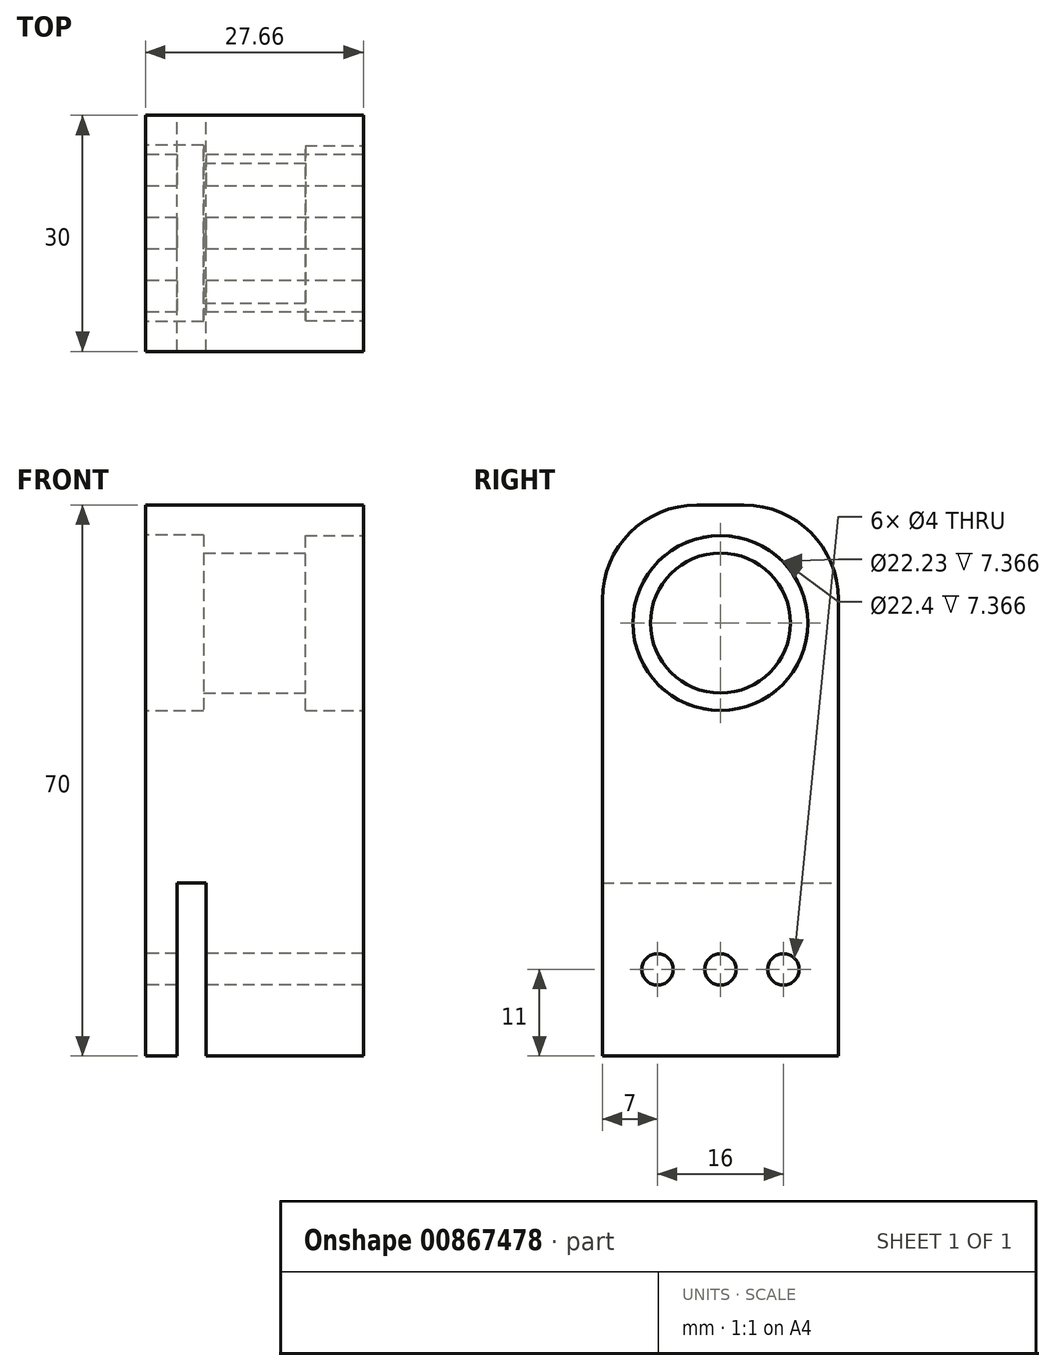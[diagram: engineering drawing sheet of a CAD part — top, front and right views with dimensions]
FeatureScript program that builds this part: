
annotation { "Feature Type Name" : "Feature", "Feature Type Description" : "" }
export const myFeature = defineFeature(function(context is Context, id is Id, definition is map)
    precondition{}
    {
        {
            var Q0;
            Q0=qCreatedBy(makeId("Front.planeOp"),FACE);
            var sketch = newSketch(context, id + "F0", { "sketchPlane" : qUnion([Q0])});
            skLineSegment(sketch, "E0.bottom", {"start": v(13.83, -27.5) * mm, "end": v(-13.82, -27.5) * mm});
            skLineSegment(sketch, "E0.top", {"start": v(13.82, 27.5) * mm, "end": v(-13.83, 27.5) * mm});
            skLineSegment(sketch, "E0.left", {"start": v(13.83, -27.5) * mm, "end": v(13.82, 27.5) * mm});
            skLineSegment(sketch, "E0.right", {"start": v(-13.82, -27.5) * mm, "end": v(-13.83, 27.5) * mm});
            skPoint(sketch, "E0.middle", {"position": v(0, 0) * mm});
            skLineSegment(sketch, "E1.bottom", {"start": v(-13.82, -27.5) * mm, "end": v(-9.82, -27.5) * mm});
            skLineSegment(sketch, "E1.top", {"start": v(-13.82, -5.5) * mm, "end": v(-9.82, -5.5) * mm, "construction": true});
            skLineSegment(sketch, "E1.left", {"start": v(-13.82, -27.5) * mm, "end": v(-13.82, -5.5) * mm});
            skLineSegment(sketch, "E1.right", {"start": v(-9.82, -27.5) * mm, "end": v(-9.82, -5.5) * mm});
            skLineSegment(sketch, "E2.bottom", {"start": v(-9.82, -27.5) * mm, "end": v(-6.17, -27.5) * mm});
            skLineSegment(sketch, "E2.top", {"start": v(-9.82, -5.5) * mm, "end": v(-6.17, -5.5) * mm});
            skLineSegment(sketch, "E2.right", {"start": v(-6.17, -27.5) * mm, "end": v(-6.17, -5.5) * mm});
            skLineSegment(sketch, "E3.bottom", {"start": v(-13.83, 27.5) * mm, "end": v(13.82, 27.5) * mm});
            skLineSegment(sketch, "E3.top", {"start": v(-13.83, 42.5) * mm, "end": v(13.82, 42.5) * mm});
            skLineSegment(sketch, "E3.left", {"start": v(-13.83, 27.5) * mm, "end": v(-13.83, 42.5) * mm});
            skLineSegment(sketch, "E3.right", {"start": v(13.82, 27.5) * mm, "end": v(13.82, 42.5) * mm});
            skSolve(sketch);
        }
        {
            var Q0;
            {var subQ1=sQuery(id+"F0.wireOp",EDGE,"E0.top");Q0=makeQuery(id+"F0.imprint","IMPRINT",FACE,{"disambiguationData":[TD([[makeQuery(id+"F0.imprint","IMPRINT",EDGE,{"derivedFrom":subQ1}),1.0]])]});}
            var Q1;
            Q1=makeQuery(id+"F0.imprint","IMPRINT",FACE,{"disambiguationData":[TD([[makeQuery(id+"F0.imprint","IMPRINT",EDGE,{"derivedFrom":sQuery(id+"F0.wireOp",EDGE,"E0.top")}),-1.0]])]});
            extrude(context, id + "F1", {"entities" : qUnion([Q0, Q1]), "endBound" : BoundingType.SYMMETRIC, "depth" : 30 * mm, "offsetDistance" : 25 * mm});
        }
        {
            var Q0;
            Q0=makeQuery(id+"F1.opExtrude","SWEPT_FACE",FACE,{"disambiguationData":[OSD([sQuery(id+"F0.wireOp",EDGE,"E0.left"),sQuery(id+"F0.wireOp",EDGE,"E3.right")])]});
            var sketch = newSketch(context, id + "F2", { "sketchPlane" : qUnion([Q0])});
            skLineSegment(sketch, "E4", {"start": v(0, 42.5) * mm, "end": v(0, 27.5) * mm});
            skCircle(sketch, "E5", {"center": v(0, 27.5) * mm, "radius": 11.11 * mm});
            skCircle(sketch, "E6", {"center": v(0, 27.5) * mm, "radius": 8.9 * mm});
            skSolve(sketch);
        }
        {
            var Q0;
            Q0=makeQuery(id+"F2.imprint","IMPRINT",FACE,{"disambiguationData":[TD([[makeQuery(id+"F2.imprint","IMPRINT",EDGE,{"derivedFrom":sQuery(id+"F2.wireOp",EDGE,"E5")}),1.0]])]});
            extrude(context, id + "F3", {"entities" : qUnion([Q0]), "operationType" : NewBodyOperationType.REMOVE, "oppositeDirection" : true, "depth" : 7.37 * mm, "offsetDistance" : 25 * mm});
        }
        {
            var Q0;
            Q0=makeQuery(id+"F3.boolean.opBoolean","SPLIT",FACE,{"disambiguationData":[TD([makeQuery(id+"F3.opExtrude","SWEPT_FACE",FACE,{"disambiguationData":[OSD([sQuery(id+"F2.wireOp",EDGE,"E6")])]})])],"derivedFrom":makeQuery(id+"F1.opExtrude","SWEPT_FACE",FACE,{"disambiguationData":[OSD([sQuery(id+"F0.wireOp",EDGE,"E0.left"),sQuery(id+"F0.wireOp",EDGE,"E3.right")])]})});
            extrude(context, id + "F4", {"entities" : qUnion([Q0]), "operationType" : NewBodyOperationType.REMOVE, "oppositeDirection" : true, "depth" : 40 * mm, "offsetDistance" : 25 * mm});
        }
        {
            var Q0;
            Q0=makeQuery(id+"F1.opExtrude","SWEPT_FACE",FACE,{"disambiguationData":[OSD([sQuery(id+"F0.wireOp",EDGE,"E0.right"),sQuery(id+"F0.wireOp",EDGE,"E3.left")])]});
            var sketch = newSketch(context, id + "F5", { "sketchPlane" : qUnion([Q0])});
            skLineSegment(sketch, "E7", {"start": v(0, 42.5) * mm, "end": v(0, 27.5) * mm});
            skCircle(sketch, "E8", {"center": v(0, 27.5) * mm, "radius": 11.2 * mm});
            skSolve(sketch);
        }
        {
            var Q0;
            Q0=makeQuery(id+"F5.imprint","IMPRINT",FACE,{"disambiguationData":[TD([[makeQuery(id+"F5.imprint","IMPRINT",EDGE,{"derivedFrom":sQuery(id+"F5.wireOp",EDGE,"E8")}),1.0]])]});
            extrude(context, id + "F6", {"entities" : qUnion([Q0]), "operationType" : NewBodyOperationType.REMOVE, "oppositeDirection" : true, "depth" : 7.37 * mm, "offsetDistance" : 25 * mm});
        }
        {
            var Q0;
            Q0=makeQuery(id+"F1.opExtrude","CAP_EDGE",EDGE,{"disambiguationData":[OSD([sQuery(id+"F0.wireOp",EDGE,"E3.top")])],"isStart":true});
            var Q1;
            Q1=makeQuery(id+"F1.opExtrude","CAP_EDGE",EDGE,{"disambiguationData":[OSD([sQuery(id+"F0.wireOp",EDGE,"E3.top")])],"isStart":false});
            fillet(context, id + "F7", {"entities" : qUnion([Q0, Q1]), "radius" : 12 * mm, "tangentPropagation" : true, "allowEdgeOverflow" : false});
        }
        {
            var Q0;
            Q0=makeQuery(id+"F1.opExtrude","SWEPT_FACE",FACE,{"disambiguationData":[OSD([sQuery(id+"F0.wireOp",EDGE,"E0.right"),sQuery(id+"F0.wireOp",EDGE,"E3.left")])]});
            var sketch = newSketch(context, id + "F8", { "sketchPlane" : qUnion([Q0])});
            skLineSegment(sketch, "E9", {"start": v(0, -27.5) * mm, "end": v(0, -16.5) * mm});
            skCircle(sketch, "E10", {"center": v(0, -16.5) * mm, "radius": 2 * mm});
            skLineSegment(sketch, "E11", {"start": v(0, -16.5) * mm, "end": v(-8, -16.5) * mm});
            skLineSegment(sketch, "E12", {"start": v(0, -16.5) * mm, "end": v(8, -16.5) * mm});
            skCircle(sketch, "E13", {"center": v(-8, -16.5) * mm, "radius": 2 * mm});
            skCircle(sketch, "E14", {"center": v(8, -16.5) * mm, "radius": 2 * mm});
            skSolve(sketch);
        }
        {
            var Q0;
            Q0=makeQuery(id+"F8.imprint","IMPRINT",FACE,{"disambiguationData":[TD([[makeQuery(id+"F8.imprint","IMPRINT",EDGE,{"derivedFrom":sQuery(id+"F8.wireOp",EDGE,"E10")}),1.0]])]});
            var Q1;
            Q1=makeQuery(id+"F8.imprint","IMPRINT",FACE,{"disambiguationData":[TD([[makeQuery(id+"F8.imprint","IMPRINT",EDGE,{"derivedFrom":sQuery(id+"F8.wireOp",EDGE,"E13")}),1.0]])]});
            var Q2;
            Q2=makeQuery(id+"F8.imprint","IMPRINT",FACE,{"disambiguationData":[TD([[makeQuery(id+"F8.imprint","IMPRINT",EDGE,{"derivedFrom":sQuery(id+"F8.wireOp",EDGE,"E14")}),1.0]])]});
            extrude(context, id + "F9", {"entities" : qUnion([Q0, Q1, Q2]), "operationType" : NewBodyOperationType.REMOVE, "oppositeDirection" : true, "depth" : 30 * mm, "offsetDistance" : 25 * mm});
        }
    });
